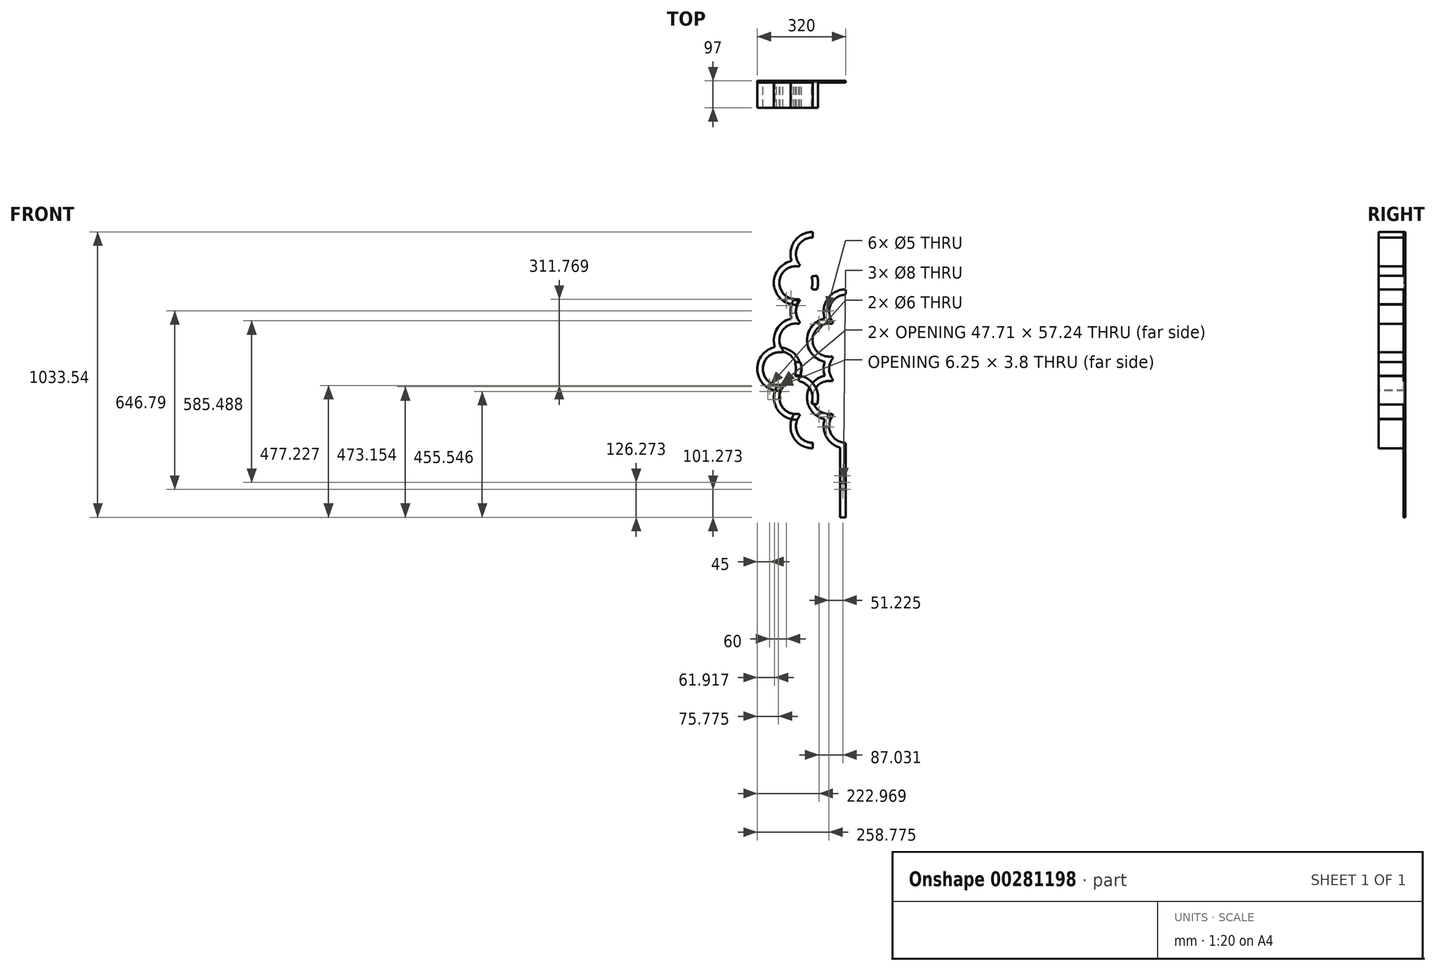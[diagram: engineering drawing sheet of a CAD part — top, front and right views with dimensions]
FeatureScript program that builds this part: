
annotation { "Feature Type Name" : "Feature", "Feature Type Description" : "" }
export const myFeature = defineFeature(function(context is Context, id is Id, definition is map)
    precondition{}
    {
        {
            var Q0;
            Q0=qCreatedBy(makeId("Front.planeOp"),FACE);
            var sketch = newSketch(context, id + "F0", { "sketchPlane" : qUnion([Q0])});
            skCircle(sketch, "E0.1.0.0", {"center": v(-79.6, 28.75) * mm, "radius": 60 * mm, "construction": true});
            skCircle(sketch, "E0.2.0.0", {"center": v(40.4, 28.75) * mm, "radius": 60 * mm, "construction": true});
            skCircle(sketch, "E0.3.0.0", {"center": v(160.4, 28.75) * mm, "radius": 60 * mm, "construction": true});
            skLineSegment(sketch, "E0.direction1", {"start": v(-199.6, 28.75) * mm, "end": v(-79.6, 28.75) * mm, "construction": true});
            skCircle(sketch, "E1", {"center": v(-139.6, 132.68) * mm, "radius": 60 * mm, "construction": true});
            skCircle(sketch, "E2.1.0.0", {"center": v(-19.6, 132.68) * mm, "radius": 60 * mm, "construction": true});
            skCircle(sketch, "E2.2.0.0", {"center": v(100.4, 132.68) * mm, "radius": 60 * mm, "construction": true});
            skCircle(sketch, "E2.3.0.0", {"center": v(220.4, 132.68) * mm, "radius": 60 * mm, "construction": true});
            skLineSegment(sketch, "E2.direction1", {"start": v(-139.6, 132.68) * mm, "end": v(-19.6, 132.68) * mm, "construction": true});
            skCircle(sketch, "E3", {"center": v(-199.6, 236.6) * mm, "radius": 60 * mm, "construction": true});
            skCircle(sketch, "E4", {"center": v(-139.6, 340.52) * mm, "radius": 60 * mm, "construction": true});
            skCircle(sketch, "E5.1.0.0", {"center": v(-79.6, 236.6) * mm, "radius": 60 * mm, "construction": true});
            skCircle(sketch, "E5.1.0.1", {"center": v(-19.6, 340.52) * mm, "radius": 60 * mm, "construction": true});
            skCircle(sketch, "E5.2.0.0", {"center": v(40.4, 236.6) * mm, "radius": 60 * mm, "construction": true});
            skCircle(sketch, "E5.2.0.1", {"center": v(100.4, 340.52) * mm, "radius": 60 * mm, "construction": true});
            skCircle(sketch, "E5.3.0.0", {"center": v(160.4, 236.6) * mm, "radius": 60 * mm, "construction": true});
            skCircle(sketch, "E5.3.0.1", {"center": v(220.4, 340.52) * mm, "radius": 60 * mm, "construction": true});
            skLineSegment(sketch, "E5.direction1", {"start": v(-199.6, 236.6) * mm, "end": v(-79.6, 236.6) * mm, "construction": true});
            skCircle(sketch, "E6.0.4.0", {"center": v(280.4, 28.75) * mm, "radius": 60 * mm, "construction": true});
            skCircle(sketch, "E7.0.4.0", {"center": v(340.4, 132.68) * mm, "radius": 60 * mm, "construction": true});
            skCircle(sketch, "E8.0.4.0", {"center": v(280.4, 236.6) * mm, "radius": 60 * mm, "construction": true});
            skCircle(sketch, "E8.2.4.0", {"center": v(340.4, 340.52) * mm, "radius": 60 * mm, "construction": true});
            skCircle(sketch, "E9.1.0.0", {"center": v(-79.6, 444.44) * mm, "radius": 60 * mm, "construction": true});
            skCircle(sketch, "E9.2.0.0", {"center": v(40.4, 444.44) * mm, "radius": 60 * mm, "construction": true});
            skCircle(sketch, "E9.3.0.0", {"center": v(160.4, 444.44) * mm, "radius": 60 * mm, "construction": true});
            skCircle(sketch, "E9.4.0.0", {"center": v(280.4, 444.44) * mm, "radius": 60 * mm, "construction": true});
            skLineSegment(sketch, "E9.direction1", {"start": v(-199.6, 444.44) * mm, "end": v(-79.6, 444.44) * mm, "construction": true});
            skCircle(sketch, "E10", {"center": v(-139.6, 548.37) * mm, "radius": 60 * mm, "construction": true});
            skCircle(sketch, "E11.1.0.0", {"center": v(-19.6, 548.37) * mm, "radius": 60 * mm, "construction": true});
            skCircle(sketch, "E11.1.0.1", {"center": v(-79.6, 652.3) * mm, "radius": 60 * mm, "construction": true});
            skCircle(sketch, "E11.2.0.0", {"center": v(100.4, 548.37) * mm, "radius": 60 * mm, "construction": true});
            skCircle(sketch, "E11.2.0.1", {"center": v(40.4, 652.3) * mm, "radius": 60 * mm, "construction": true});
            skCircle(sketch, "E11.3.0.0", {"center": v(220.4, 548.37) * mm, "radius": 60 * mm, "construction": true});
            skCircle(sketch, "E11.3.0.1", {"center": v(160.4, 652.3) * mm, "radius": 60 * mm, "construction": true});
            skCircle(sketch, "E11.4.0.0", {"center": v(340.4, 548.37) * mm, "radius": 60 * mm, "construction": true});
            skCircle(sketch, "E11.4.0.1", {"center": v(280.4, 652.3) * mm, "radius": 60 * mm, "construction": true});
            skLineSegment(sketch, "E11.direction1", {"start": v(-139.6, 548.37) * mm, "end": v(-19.6, 548.37) * mm, "construction": true});
            skSolve(sketch);
        }
        {
            var Q0;
            Q0=qCreatedBy(makeId("Front.planeOp"),FACE);
            var sketch = newSketch(context, id + "F1", { "sketchPlane" : qUnion([Q0])});
            skCircle(sketch, "E12.0", {"center": v(-199.6, 236.6) * mm, "radius": 60 * mm});
            skCircle(sketch, "E13.0", {"center": v(-139.6, 340.52) * mm, "radius": 60 * mm});
            skCircle(sketch, "E14.0", {"center": v(-139.6, 132.68) * mm, "radius": 60 * mm});
            skCircle(sketch, "E15.0", {"center": v(-79.6, 28.75) * mm, "radius": 60 * mm});
            skCircle(sketch, "E16.0", {"center": v(-139.6, 548.37) * mm, "radius": 60 * mm});
            skCircle(sketch, "E17.0", {"center": v(-79.6, 444.44) * mm, "radius": 60 * mm});
            skCircle(sketch, "E18.0", {"center": v(-79.6, 652.3) * mm, "radius": 60 * mm});
            skCircle(sketch, "E19", {"center": v(-79.6, 652.3) * mm, "radius": 80 * mm});
            skCircle(sketch, "E20", {"center": v(-139.6, 548.37) * mm, "radius": 80 * mm});
            skCircle(sketch, "E21", {"center": v(-79.6, 444.44) * mm, "radius": 80 * mm});
            skCircle(sketch, "E22", {"center": v(-139.6, 340.52) * mm, "radius": 80 * mm});
            skCircle(sketch, "E23", {"center": v(-199.6, 236.6) * mm, "radius": 80 * mm});
            skCircle(sketch, "E24", {"center": v(-139.6, 132.68) * mm, "radius": 80 * mm});
            skCircle(sketch, "E25", {"center": v(-79.6, 28.75) * mm, "radius": 80 * mm});
            skLineSegment(sketch, "E26", {"start": v(-79.6, 28.75) * mm, "end": v(-79.6, -51.25) * mm});
            skLineSegment(sketch, "E27", {"start": v(-79.6, 652.3) * mm, "end": v(-79.6, 732.3) * mm});
            skSolve(sketch);
        }
        {
            var Q0;
            {var subQ0=sQuery(id+"F1.wireOp",EDGE,"E27");var subQ1=sQuery(id+"F1.wireOp",EDGE,"E18.0");var subQ2=makeQuery(id+"F1.imprint","INTERSECT",VERTEX,{"derivedFrom":[subQ1,subQ0]});Q0=makeQuery(id+"F1.imprint","IMPRINT",FACE,{"disambiguationData":[TD([[makeQuery(id+"F1.imprint","IMPRINT",EDGE,{"disambiguationData":[TD([[subQ2,-1.0]])],"derivedFrom":subQ1}),-1.0]])]});}
            var Q1;
            {var subQ0=sQuery(id+"F1.wireOp",EDGE,"E18.0");var subQ1=sQuery(id+"F1.wireOp",EDGE,"E16.0");var subQ2=makeQuery(id+"F1.imprint","INTERSECT",VERTEX,{"derivedFrom":[subQ1,subQ0]});Q1=makeQuery(id+"F1.imprint","IMPRINT",FACE,{"disambiguationData":[TD([[makeQuery(id+"F1.imprint","IMPRINT",EDGE,{"disambiguationData":[TD([[subQ2,-1.0]])],"derivedFrom":subQ1}),-1.0]])]});}
            var Q2;
            {var subQ0=sQuery(id+"F1.wireOp",EDGE,"E19");var subQ1=sQuery(id+"F1.wireOp",EDGE,"E16.0");var subQ2=makeQuery(id+"F1.imprint","INTERSECT",VERTEX,{"disambiguationData":[OD(1.0)],"derivedFrom":[subQ1,subQ0]});Q2=makeQuery(id+"F1.imprint","IMPRINT",FACE,{"disambiguationData":[TD([[makeQuery(id+"F1.imprint","IMPRINT",EDGE,{"disambiguationData":[TD([[subQ2,-1.0]])],"derivedFrom":subQ1}),-1.0]])]});}
            var Q3;
            {var subQ0=sQuery(id+"F1.wireOp",EDGE,"E20");var subQ1=sQuery(id+"F1.wireOp",EDGE,"E17.0");var subQ2=makeQuery(id+"F1.imprint","INTERSECT",VERTEX,{"disambiguationData":[OD(1.0)],"derivedFrom":[subQ1,subQ0]});Q3=makeQuery(id+"F1.imprint","IMPRINT",FACE,{"disambiguationData":[TD([[makeQuery(id+"F1.imprint","IMPRINT",EDGE,{"disambiguationData":[TD([[subQ2,-1.0]])],"derivedFrom":subQ1}),-1.0]])]});}
            var Q4;
            {var subQ0=sQuery(id+"F1.wireOp",EDGE,"E21");var subQ1=sQuery(id+"F1.wireOp",EDGE,"E16.0");var subQ2=makeQuery(id+"F1.imprint","INTERSECT",VERTEX,{"disambiguationData":[OD(0.0)],"derivedFrom":[subQ1,subQ0]});Q4=makeQuery(id+"F1.imprint","IMPRINT",FACE,{"disambiguationData":[TD([[makeQuery(id+"F1.imprint","IMPRINT",EDGE,{"disambiguationData":[TD([[subQ2,-1.0]])],"derivedFrom":subQ1}),-1.0]])]});}
            var Q5;
            {var subQ0=sQuery(id+"F1.wireOp",EDGE,"E21");var subQ1=sQuery(id+"F1.wireOp",EDGE,"E13.0");var subQ2=makeQuery(id+"F1.imprint","INTERSECT",VERTEX,{"disambiguationData":[OD(1.0)],"derivedFrom":[subQ1,subQ0]});Q5=makeQuery(id+"F1.imprint","IMPRINT",FACE,{"disambiguationData":[TD([[makeQuery(id+"F1.imprint","IMPRINT",EDGE,{"disambiguationData":[TD([[subQ2,-1.0]])],"derivedFrom":subQ1}),-1.0]])]});}
            var Q6;
            {var subQ0=sQuery(id+"F1.wireOp",EDGE,"E17.0");var subQ1=sQuery(id+"F1.wireOp",EDGE,"E13.0");var subQ2=makeQuery(id+"F1.imprint","INTERSECT",VERTEX,{"derivedFrom":[subQ1,subQ0]});Q6=makeQuery(id+"F1.imprint","IMPRINT",FACE,{"disambiguationData":[TD([[makeQuery(id+"F1.imprint","IMPRINT",EDGE,{"disambiguationData":[TD([[subQ2,-1.0]])],"derivedFrom":subQ1}),-1.0]])]});}
            var Q7;
            {var subQ0=sQuery(id+"F1.wireOp",EDGE,"E13.0");var subQ1=sQuery(id+"F1.wireOp",EDGE,"E12.0");var subQ2=makeQuery(id+"F1.imprint","INTERSECT",VERTEX,{"derivedFrom":[subQ1,subQ0]});Q7=makeQuery(id+"F1.imprint","IMPRINT",FACE,{"disambiguationData":[TD([[makeQuery(id+"F1.imprint","IMPRINT",EDGE,{"disambiguationData":[TD([[subQ2,-1.0]])],"derivedFrom":subQ1}),-1.0]])]});}
            var Q8;
            {var subQ0=sQuery(id+"F1.wireOp",EDGE,"E22");var subQ1=sQuery(id+"F1.wireOp",EDGE,"E12.0");var subQ2=makeQuery(id+"F1.imprint","INTERSECT",VERTEX,{"disambiguationData":[OD(1.0)],"derivedFrom":[subQ1,subQ0]});Q8=makeQuery(id+"F1.imprint","IMPRINT",FACE,{"disambiguationData":[TD([[makeQuery(id+"F1.imprint","IMPRINT",EDGE,{"disambiguationData":[TD([[subQ2,-1.0]])],"derivedFrom":subQ1}),-1.0]])]});}
            var Q9;
            {var subQ0=sQuery(id+"F1.wireOp",EDGE,"E23");var subQ1=sQuery(id+"F1.wireOp",EDGE,"E14.0");var subQ2=makeQuery(id+"F1.imprint","INTERSECT",VERTEX,{"disambiguationData":[OD(1.0)],"derivedFrom":[subQ1,subQ0]});Q9=makeQuery(id+"F1.imprint","IMPRINT",FACE,{"disambiguationData":[TD([[makeQuery(id+"F1.imprint","IMPRINT",EDGE,{"disambiguationData":[TD([[subQ2,-1.0]])],"derivedFrom":subQ1}),-1.0]])]});}
            var Q10;
            {var subQ0=sQuery(id+"F1.wireOp",EDGE,"E26");var subQ1=sQuery(id+"F1.wireOp",EDGE,"E15.0");var subQ2=makeQuery(id+"F1.imprint","INTERSECT",VERTEX,{"derivedFrom":[subQ1,subQ0]});Q10=makeQuery(id+"F1.imprint","IMPRINT",FACE,{"disambiguationData":[TD([[makeQuery(id+"F1.imprint","IMPRINT",EDGE,{"disambiguationData":[TD([[subQ2,1.0]])],"derivedFrom":subQ1}),-1.0]])]});}
            var Q11;
            {var subQ0=sQuery(id+"F1.wireOp",EDGE,"E25");var subQ1=sQuery(id+"F1.wireOp",EDGE,"E14.0");var subQ2=makeQuery(id+"F1.imprint","INTERSECT",VERTEX,{"disambiguationData":[OD(0.0)],"derivedFrom":[subQ1,subQ0]});Q11=makeQuery(id+"F1.imprint","IMPRINT",FACE,{"disambiguationData":[TD([[makeQuery(id+"F1.imprint","IMPRINT",EDGE,{"disambiguationData":[TD([[subQ2,-1.0]])],"derivedFrom":subQ1}),-1.0]])]});}
            var Q12;
            {var subQ0=sQuery(id+"F1.wireOp",EDGE,"E24");var subQ1=sQuery(id+"F1.wireOp",EDGE,"E12.0");var subQ2=makeQuery(id+"F1.imprint","INTERSECT",VERTEX,{"disambiguationData":[OD(0.0)],"derivedFrom":[subQ1,subQ0]});Q12=makeQuery(id+"F1.imprint","IMPRINT",FACE,{"disambiguationData":[TD([[makeQuery(id+"F1.imprint","IMPRINT",EDGE,{"disambiguationData":[TD([[subQ2,-1.0]])],"derivedFrom":subQ1}),-1.0]])]});}
            extrude(context, id + "F2", {"entities" : qUnion([Q0, Q1, Q2, Q3, Q4, Q5, Q6, Q7, Q8, Q9, Q10, Q11, Q12]), "depth" : 97 * mm});
        }
        {
            var Q0;
            Q0=makeQuery(id+"F2.opExtrude","SWEPT_EDGE",EDGE,{"disambiguationData":[OSD([sQuery(id+"F1.wireOp",EDGE,"E16.0"),sQuery(id+"F1.wireOp",EDGE,"E18.0")])]});
            var Q1;
            Q1=makeQuery(id+"F2.opExtrude","SWEPT_EDGE",EDGE,{"disambiguationData":[OSD([sQuery(id+"F1.wireOp",EDGE,"E16.0"),sQuery(id+"F1.wireOp",EDGE,"E17.0")])]});
            var Q2;
            Q2=makeQuery(id+"F2.opExtrude","SWEPT_EDGE",EDGE,{"disambiguationData":[OSD([sQuery(id+"F1.wireOp",EDGE,"E13.0"),sQuery(id+"F1.wireOp",EDGE,"E17.0")])]});
            var Q3;
            Q3=makeQuery(id+"F2.opExtrude","SWEPT_EDGE",EDGE,{"disambiguationData":[OSD([sQuery(id+"F1.wireOp",EDGE,"E12.0"),sQuery(id+"F1.wireOp",EDGE,"E13.0")])]});
            var Q4;
            Q4=makeQuery(id+"F2.opExtrude","SWEPT_EDGE",EDGE,{"disambiguationData":[OSD([sQuery(id+"F1.wireOp",EDGE,"E12.0"),sQuery(id+"F1.wireOp",EDGE,"E14.0")])]});
            var Q5;
            Q5=makeQuery(id+"F2.opExtrude","SWEPT_EDGE",EDGE,{"disambiguationData":[OSD([sQuery(id+"F1.wireOp",EDGE,"E14.0"),sQuery(id+"F1.wireOp",EDGE,"E15.0")])]});
            var Q6;
            Q6=makeQuery(id+"F2.opExtrude","SWEPT_EDGE",EDGE,{"disambiguationData":[OSD([sQuery(id+"F1.wireOp",EDGE,"E19"),sQuery(id+"F1.wireOp",EDGE,"E20")])]});
            var Q7;
            Q7=makeQuery(id+"F2.opExtrude","SWEPT_EDGE",EDGE,{"disambiguationData":[OSD([sQuery(id+"F1.wireOp",EDGE,"E21"),sQuery(id+"F1.wireOp",EDGE,"E22")])]});
            var Q8;
            Q8=makeQuery(id+"F2.opExtrude","SWEPT_EDGE",EDGE,{"disambiguationData":[OSD([sQuery(id+"F1.wireOp",EDGE,"E22"),sQuery(id+"F1.wireOp",EDGE,"E23")])]});
            var Q9;
            Q9=makeQuery(id+"F2.opExtrude","SWEPT_EDGE",EDGE,{"disambiguationData":[OSD([sQuery(id+"F1.wireOp",EDGE,"E20"),sQuery(id+"F1.wireOp",EDGE,"E21")])]});
            var Q10;
            Q10=makeQuery(id+"F2.opExtrude","SWEPT_EDGE",EDGE,{"disambiguationData":[OSD([sQuery(id+"F1.wireOp",EDGE,"E23"),sQuery(id+"F1.wireOp",EDGE,"E24")])]});
            var Q11;
            Q11=makeQuery(id+"F2.opExtrude","SWEPT_EDGE",EDGE,{"disambiguationData":[OSD([sQuery(id+"F1.wireOp",EDGE,"E24"),sQuery(id+"F1.wireOp",EDGE,"E25")])]});
            fillet(context, id + "F3", {"entities" : qUnion([Q0, Q1, Q2, Q3, Q4, Q5, Q6, Q7, Q8, Q9, Q10, Q11]), "radius" : 5 * mm, "tangentPropagation" : true, "allowEdgeOverflow" : false});
        }
        {
            var Q0;
            Q0=qCreatedBy(makeId("Front.planeOp"),FACE);
            var sketch = newSketch(context, id + "F4", { "sketchPlane" : qUnion([Q0])});
            skArc(sketch, "E28.0", {"start": v(-79.6, 732.3) * mm, "mid": v(-144.55, 698.98) * mm, "end": v(-155.42, 626.79) * mm});
            skArc(sketch, "E28.1", {"start": v(-79.6, 712.3) * mm, "mid": v(-133.37, 678.88) * mm, "end": v(-127.27, 615.86) * mm});
            skArc(sketch, "E28.2", {"start": v(-131.88, 607.87) * mm, "mid": v(-199.6, 548.37) * mm, "end": v(-131.88, 488.86) * mm});
            skArc(sketch, "E28.5", {"start": v(-127.27, 480.87) * mm, "mid": v(-139.6, 444.44) * mm, "end": v(-127.27, 408.02) * mm});
            skArc(sketch, "E28.6", {"start": v(-155.42, 418.94) * mm, "mid": v(-208.87, 380.52) * mm, "end": v(-215.42, 315.02) * mm});
            skArc(sketch, "E28.7", {"start": v(-131.88, 400.02) * mm, "mid": v(-191.55, 370.52) * mm, "end": v(-187.27, 304.1) * mm});
            skArc(sketch, "E28.8", {"start": v(-215.42, 315.02) * mm, "mid": v(-279.6, 236.6) * mm, "end": v(-215.42, 158.18) * mm});
            skArc(sketch, "E28.9", {"start": v(-191.88, 296.1) * mm, "mid": v(-259.6, 236.6) * mm, "end": v(-191.88, 177.1) * mm});
            skArc(sketch, "E28.10", {"start": v(-215.42, 158.18) * mm, "mid": v(-208.87, 92.68) * mm, "end": v(-155.42, 54.26) * mm});
            skArc(sketch, "E28.11", {"start": v(-187.27, 169.1) * mm, "mid": v(-191.55, 102.68) * mm, "end": v(-131.88, 73.17) * mm});
            skArc(sketch, "E28.12", {"start": v(-155.42, 54.26) * mm, "mid": v(-144.55, -17.94) * mm, "end": v(-79.6, -51.25) * mm});
            skArc(sketch, "E28.13", {"start": v(-127.27, 65.18) * mm, "mid": v(-133.37, 2.16) * mm, "end": v(-79.6, -31.25) * mm});
            skLineSegment(sketch, "E29.0", {"start": v(-79.6, 652.3) * mm, "end": v(-79.6, 732.3) * mm});
            skLineSegment(sketch, "E30.0", {"start": v(-79.6, -31.25) * mm, "end": v(-79.6, -51.25) * mm});
            skArc(sketch, "E31.trimOffspring", {"start": v(-155.42, 626.79) * mm, "mid": v(-219.6, 548.37) * mm, "end": v(-155.42, 469.95) * mm});
            skArc(sketch, "E32.trimOffspring", {"start": v(-155.42, 469.95) * mm, "mid": v(-159.6, 444.44) * mm, "end": v(-155.42, 418.94) * mm});
            skPoint(sketch, "E33.visualSharp", {"position": v(-109.6, 496.4) * mm});
            skCircle(sketch, "E34", {"center": v(-199.6, 236.6) * mm, "radius": 70 * mm, "construction": true});
            skCircle(sketch, "E35", {"center": v(-139.6, 132.68) * mm, "radius": 70 * mm, "construction": true});
            skPoint(sketch, "E36.visualSharp", {"position": v(-169.6, 184.64) * mm});
            skPoint(sketch, "E37.visualSharp", {"position": v(-109.6, 80.71) * mm});
            skArc(sketch, "E37.filletArc", {"start": v(-127.27, 65.18) * mm, "mid": v(-126.91, 70.71) * mm, "end": v(-131.88, 73.17) * mm});
            skArc(sketch, "E38.filletArc", {"start": v(-187.27, 169.1) * mm, "mid": v(-186.91, 174.64) * mm, "end": v(-191.88, 177.1) * mm});
            skPoint(sketch, "E39.visualSharp", {"position": v(-169.6, 288.56) * mm});
            skArc(sketch, "E39.filletArc", {"start": v(-191.88, 296.1) * mm, "mid": v(-186.91, 298.56) * mm, "end": v(-187.27, 304.1) * mm});
            skPoint(sketch, "E40.visualSharp", {"position": v(-109.6, 392.48) * mm});
            skArc(sketch, "E40.filletArc", {"start": v(-131.88, 400.02) * mm, "mid": v(-126.91, 402.48) * mm, "end": v(-127.27, 408.02) * mm});
            skArc(sketch, "E41.filletArc", {"start": v(-127.27, 480.87) * mm, "mid": v(-126.91, 486.4) * mm, "end": v(-131.88, 488.86) * mm});
            skPoint(sketch, "E42.visualSharp", {"position": v(-109.6, 600.33) * mm});
            skArc(sketch, "E42.filletArc", {"start": v(-131.88, 607.87) * mm, "mid": v(-126.91, 610.33) * mm, "end": v(-127.27, 615.86) * mm});
            skCircle(sketch, "E43", {"center": v(-79.6, 444.44) * mm, "radius": 63 * mm});
            skCircle(sketch, "E44", {"center": v(-79.6, 444.44) * mm, "radius": 77 * mm});
            skCircle(sketch, "E45", {"center": v(-199.6, 236.6) * mm, "radius": 63 * mm});
            skCircle(sketch, "E46", {"center": v(-199.6, 236.6) * mm, "radius": 77 * mm});
            skCircle(sketch, "E47", {"center": v(-139.6, 132.68) * mm, "radius": 63 * mm});
            skCircle(sketch, "E48", {"center": v(-139.6, 132.68) * mm, "radius": 77 * mm});
            skCircle(sketch, "E49", {"center": v(-200.82, 166.6) * mm, "radius": 7 * mm});
            skCircle(sketch, "E50", {"center": v(-139.6, 548.37) * mm, "radius": 63 * mm});
            skCircle(sketch, "E51", {"center": v(-139.6, 548.37) * mm, "radius": 77 * mm});
            skCircle(sketch, "E52", {"center": v(-79.6, 444.44) * mm, "radius": 70 * mm, "construction": true});
            skCircle(sketch, "E53", {"center": v(-139.6, 548.37) * mm, "radius": 70 * mm, "construction": true});
            skCircle(sketch, "E54", {"center": v(-140.82, 478.38) * mm, "radius": 7 * mm});
            skArc(sketch, "E55", {"start": v(-156.6, 444.44) * mm, "mid": v(-149.6, 437.44) * mm, "end": v(-142.6, 444.44) * mm});
            skArc(sketch, "E56", {"start": v(-171.1, 493.8) * mm, "mid": v(-180.65, 491.25) * mm, "end": v(-178.1, 481.68) * mm});
            skArc(sketch, "E57", {"start": v(-216.6, 132.68) * mm, "mid": v(-209.6, 125.68) * mm, "end": v(-202.6, 132.68) * mm});
            skArc(sketch, "E58", {"start": v(-231.1, 182.04) * mm, "mid": v(-240.65, 179.48) * mm, "end": v(-238.1, 169.91) * mm});
            skCircle(sketch, "E59", {"center": v(-174.6, 487.75) * mm, "radius": 3 * mm});
            skCircle(sketch, "E60", {"center": v(-234.6, 175.98) * mm, "radius": 3 * mm});
            skSolve(sketch);
        }
        {
            var Q0;
            {var subQ8=sQuery(id+"F4.wireOp",EDGE,"E28.0");Q0=makeQuery(id+"F4.imprint","IMPRINT",FACE,{"disambiguationData":[TD([[makeQuery(id+"F4.imprint","IMPRINT",EDGE,{"derivedFrom":subQ8}),1.0]])]});}
            var Q1;
            {var subQ0=sQuery(id+"F4.wireOp",EDGE,"E56");Q1=makeQuery(id+"F4.imprint","IMPRINT",FACE,{"disambiguationData":[TD([[makeQuery(id+"F4.imprint","IMPRINT",EDGE,{"derivedFrom":subQ0}),-1.0]])]});}
            var Q2;
            {var subQ2=sQuery(id+"F4.wireOp",EDGE,"E42.filletArc");var subQ4=sQuery(id+"F4.wireOp",EDGE,"E28.2");var subQ5=makeQuery(id+"F4.imprint","INTERSECT",VERTEX,{"derivedFrom":[subQ4,subQ2]});Q2=makeQuery(id+"F4.imprint","IMPRINT",FACE,{"disambiguationData":[TD([[makeQuery(id+"F4.imprint","IMPRINT",EDGE,{"disambiguationData":[TD([[subQ5,-1.0]])],"derivedFrom":subQ4}),-1.0]])]});}
            var Q3;
            {var subQ4=sQuery(id+"F4.wireOp",EDGE,"E28.2");var subQ6=sQuery(id+"F4.wireOp",EDGE,"E41.filletArc");var subQ7=makeQuery(id+"F4.imprint","INTERSECT",VERTEX,{"derivedFrom":[subQ4,subQ6]});Q3=makeQuery(id+"F4.imprint","IMPRINT",FACE,{"disambiguationData":[TD([[makeQuery(id+"F4.imprint","IMPRINT",EDGE,{"disambiguationData":[TD([[subQ7,1.0]])],"derivedFrom":subQ4}),-1.0]])]});}
            var Q4;
            {var subQ0=sQuery(id+"F4.wireOp",EDGE,"E43");var subQ1=sQuery(id+"F4.wireOp",EDGE,"E41.filletArc");var subQ2=makeQuery(id+"F4.imprint","INTERSECT",VERTEX,{"derivedFrom":[subQ1,subQ0]});Q4=makeQuery(id+"F4.imprint","IMPRINT",FACE,{"disambiguationData":[TD([[makeQuery(id+"F4.imprint","IMPRINT",EDGE,{"disambiguationData":[TD([[subQ2,-1.0]])],"derivedFrom":subQ1}),1.0]])]});}
            var Q5;
            {var subQ4=sQuery(id+"F4.wireOp",EDGE,"E41.filletArc");var subQ6=sQuery(id+"F4.wireOp",EDGE,"E28.5");var subQ7=makeQuery(id+"F4.imprint","INTERSECT",VERTEX,{"derivedFrom":[subQ6,subQ4]});Q5=makeQuery(id+"F4.imprint","IMPRINT",FACE,{"disambiguationData":[TD([[makeQuery(id+"F4.imprint","IMPRINT",EDGE,{"disambiguationData":[TD([[subQ7,-1.0]])],"derivedFrom":subQ6}),-1.0]])]});}
            var Q6;
            {var subQ2=sQuery(id+"F4.wireOp",EDGE,"E40.filletArc");var subQ6=sQuery(id+"F4.wireOp",EDGE,"E28.5");var subQ7=makeQuery(id+"F4.imprint","INTERSECT",VERTEX,{"derivedFrom":[subQ6,subQ2]});Q6=makeQuery(id+"F4.imprint","IMPRINT",FACE,{"disambiguationData":[TD([[makeQuery(id+"F4.imprint","IMPRINT",EDGE,{"disambiguationData":[TD([[subQ7,1.0]])],"derivedFrom":subQ6}),-1.0]])]});}
            var Q7;
            {var subQ0=sQuery(id+"F4.wireOp",EDGE,"E55");Q7=makeQuery(id+"F4.imprint","IMPRINT",FACE,{"disambiguationData":[TD([[makeQuery(id+"F4.imprint","IMPRINT",EDGE,{"derivedFrom":subQ0}),-1.0]])]});}
            var Q8;
            {var subQ0=sQuery(id+"F4.wireOp",EDGE,"E58");Q8=makeQuery(id+"F4.imprint","IMPRINT",FACE,{"disambiguationData":[TD([[makeQuery(id+"F4.imprint","IMPRINT",EDGE,{"derivedFrom":subQ0}),-1.0]])]});}
            var Q9;
            {var subQ4=sQuery(id+"F4.wireOp",EDGE,"E39.filletArc");var subQ6=sQuery(id+"F4.wireOp",EDGE,"E28.9");var subQ7=makeQuery(id+"F4.imprint","INTERSECT",VERTEX,{"derivedFrom":[subQ6,subQ4]});Q9=makeQuery(id+"F4.imprint","IMPRINT",FACE,{"disambiguationData":[TD([[makeQuery(id+"F4.imprint","IMPRINT",EDGE,{"disambiguationData":[TD([[subQ7,-1.0]])],"derivedFrom":subQ6}),-1.0]])]});}
            var Q10;
            {var subQ4=sQuery(id+"F4.wireOp",EDGE,"E37.filletArc");var subQ5=sQuery(id+"F4.wireOp",EDGE,"E28.11");var subQ6=makeQuery(id+"F4.imprint","INTERSECT",VERTEX,{"derivedFrom":[subQ5,subQ4]});Q10=makeQuery(id+"F4.imprint","IMPRINT",FACE,{"disambiguationData":[TD([[makeQuery(id+"F4.imprint","IMPRINT",EDGE,{"disambiguationData":[TD([[subQ6,1.0]])],"derivedFrom":subQ5}),-1.0]])]});}
            var Q11;
            {var subQ1=sQuery(id+"F4.wireOp",EDGE,"E38.filletArc");var subQ5=sQuery(id+"F4.wireOp",EDGE,"E28.11");var subQ8=makeQuery(id+"F4.imprint","INTERSECT",VERTEX,{"derivedFrom":[subQ5,subQ1]});Q11=makeQuery(id+"F4.imprint","IMPRINT",FACE,{"disambiguationData":[TD([[makeQuery(id+"F4.imprint","IMPRINT",EDGE,{"disambiguationData":[TD([[subQ8,-1.0]])],"derivedFrom":subQ5}),-1.0]])]});}
            var Q12;
            {var subQ1=sQuery(id+"F4.wireOp",EDGE,"E38.filletArc");var subQ4=sQuery(id+"F4.wireOp",EDGE,"E28.9");var subQ5=makeQuery(id+"F4.imprint","INTERSECT",VERTEX,{"derivedFrom":[subQ4,subQ1]});Q12=makeQuery(id+"F4.imprint","IMPRINT",FACE,{"disambiguationData":[TD([[makeQuery(id+"F4.imprint","IMPRINT",EDGE,{"disambiguationData":[TD([[subQ5,1.0]])],"derivedFrom":subQ4}),-1.0]])]});}
            var Q13;
            {var subQ0=sQuery(id+"F4.wireOp",EDGE,"E47");var subQ1=sQuery(id+"F4.wireOp",EDGE,"E38.filletArc");var subQ2=makeQuery(id+"F4.imprint","INTERSECT",VERTEX,{"derivedFrom":[subQ1,subQ0]});Q13=makeQuery(id+"F4.imprint","IMPRINT",FACE,{"disambiguationData":[TD([[makeQuery(id+"F4.imprint","IMPRINT",EDGE,{"disambiguationData":[TD([[subQ2,-1.0]])],"derivedFrom":subQ1}),1.0]])]});}
            var Q14;
            {var subQ0=sQuery(id+"F4.wireOp",EDGE,"E57");Q14=makeQuery(id+"F4.imprint","IMPRINT",FACE,{"disambiguationData":[TD([[makeQuery(id+"F4.imprint","IMPRINT",EDGE,{"derivedFrom":subQ0}),-1.0]])]});}
            extrude(context, id + "F5", {"entities" : qUnion([Q0, Q1, Q2, Q3, Q4, Q5, Q6, Q7, Q8, Q9, Q10, Q11, Q12, Q13, Q14]), "depth" : 6 * mm});
        }
        {
            var Q0;
            {var subQ0=sQuery(id+"F4.wireOp",EDGE,"E56");Q0=makeQuery(id+"F4.imprint","IMPRINT",FACE,{"disambiguationData":[TD([[makeQuery(id+"F4.imprint","IMPRINT",EDGE,{"derivedFrom":subQ0}),1.0]])]});}
            var Q1;
            {var subQ0=sQuery(id+"F4.wireOp",EDGE,"E54");var subQ1=makeQuery(id+"F4.imprint","INTERSECT",VERTEX,{"derivedFrom":[sQuery(id+"F4.wireOp",EDGE,"E44"),subQ0]});Q1=makeQuery(id+"F4.imprint","IMPRINT",FACE,{"disambiguationData":[TD([[makeQuery(id+"F4.imprint","IMPRINT",EDGE,{"disambiguationData":[TD([[subQ1,1.0]])],"derivedFrom":subQ0}),1.0]])]});}
            var Q2;
            {var subQ6=sQuery(id+"F4.wireOp",EDGE,"E55");Q2=makeQuery(id+"F4.imprint","IMPRINT",FACE,{"disambiguationData":[TD([[makeQuery(id+"F4.imprint","IMPRINT",EDGE,{"derivedFrom":subQ6}),1.0]])]});}
            var Q3;
            {var subQ0=sQuery(id+"F4.wireOp",EDGE,"E50");var subQ1=sQuery(id+"F4.wireOp",EDGE,"E44");var subQ2=makeQuery(id+"F4.imprint","INTERSECT",VERTEX,{"disambiguationData":[OD(1.0)],"derivedFrom":[subQ1,subQ0]});Q3=makeQuery(id+"F4.imprint","IMPRINT",FACE,{"disambiguationData":[TD([[makeQuery(id+"F4.imprint","IMPRINT",EDGE,{"disambiguationData":[TD([[subQ2,-1.0]])],"derivedFrom":subQ1}),1.0]])]});}
            var Q4;
            {var subQ0=sQuery(id+"F4.wireOp",EDGE,"E54");var subQ1=sQuery(id+"F4.wireOp",EDGE,"E44");var subQ2=makeQuery(id+"F4.imprint","INTERSECT",VERTEX,{"derivedFrom":[subQ1,subQ0]});Q4=makeQuery(id+"F4.imprint","IMPRINT",FACE,{"disambiguationData":[TD([[makeQuery(id+"F4.imprint","IMPRINT",EDGE,{"disambiguationData":[TD([[subQ2,-1.0]])],"derivedFrom":subQ1}),1.0]])]});}
            var Q5;
            {var subQ0=sQuery(id+"F4.wireOp",EDGE,"E54");var subQ1=sQuery(id+"F4.wireOp",EDGE,"E43");var subQ2=makeQuery(id+"F4.imprint","INTERSECT",VERTEX,{"derivedFrom":[subQ1,subQ0]});Q5=makeQuery(id+"F4.imprint","IMPRINT",FACE,{"disambiguationData":[TD([[makeQuery(id+"F4.imprint","IMPRINT",EDGE,{"disambiguationData":[TD([[subQ2,-1.0]])],"derivedFrom":subQ1}),-1.0]])]});}
            var Q6;
            {var subQ6=sQuery(id+"F4.wireOp",EDGE,"E58");Q6=makeQuery(id+"F4.imprint","IMPRINT",FACE,{"disambiguationData":[TD([[makeQuery(id+"F4.imprint","IMPRINT",EDGE,{"derivedFrom":subQ6}),1.0]])]});}
            var Q7;
            {var subQ0=sQuery(id+"F4.wireOp",EDGE,"E49");var subQ1=makeQuery(id+"F4.imprint","INTERSECT",VERTEX,{"derivedFrom":[sQuery(id+"F4.wireOp",EDGE,"E45"),subQ0]});Q7=makeQuery(id+"F4.imprint","IMPRINT",FACE,{"disambiguationData":[TD([[makeQuery(id+"F4.imprint","IMPRINT",EDGE,{"disambiguationData":[TD([[subQ1,-1.0]])],"derivedFrom":subQ0}),1.0]])]});}
            var Q8;
            {var subQ0=sQuery(id+"F4.wireOp",EDGE,"E57");Q8=makeQuery(id+"F4.imprint","IMPRINT",FACE,{"disambiguationData":[TD([[makeQuery(id+"F4.imprint","IMPRINT",EDGE,{"derivedFrom":subQ0}),1.0]])]});}
            var Q9;
            {var subQ0=sQuery(id+"F4.wireOp",EDGE,"E48");var subQ1=sQuery(id+"F4.wireOp",EDGE,"E46");var subQ2=makeQuery(id+"F4.imprint","INTERSECT",VERTEX,{"disambiguationData":[OD(1.0)],"derivedFrom":[subQ1,subQ0]});Q9=makeQuery(id+"F4.imprint","IMPRINT",FACE,{"disambiguationData":[TD([[makeQuery(id+"F4.imprint","IMPRINT",EDGE,{"disambiguationData":[TD([[subQ2,-1.0]])],"derivedFrom":subQ1}),1.0]])]});}
            var Q10;
            {var subQ0=sQuery(id+"F4.wireOp",EDGE,"E49");var subQ1=sQuery(id+"F4.wireOp",EDGE,"E46");var subQ2=makeQuery(id+"F4.imprint","INTERSECT",VERTEX,{"derivedFrom":[subQ1,subQ0]});Q10=makeQuery(id+"F4.imprint","IMPRINT",FACE,{"disambiguationData":[TD([[makeQuery(id+"F4.imprint","IMPRINT",EDGE,{"disambiguationData":[TD([[subQ2,-1.0]])],"derivedFrom":subQ1}),1.0]])]});}
            var Q11;
            {var subQ0=sQuery(id+"F4.wireOp",EDGE,"E48");var subQ1=sQuery(id+"F4.wireOp",EDGE,"E45");var subQ2=makeQuery(id+"F4.imprint","INTERSECT",VERTEX,{"disambiguationData":[OD(0.0)],"derivedFrom":[subQ1,subQ0]});Q11=makeQuery(id+"F4.imprint","IMPRINT",FACE,{"disambiguationData":[TD([[makeQuery(id+"F4.imprint","IMPRINT",EDGE,{"disambiguationData":[TD([[subQ2,-1.0]])],"derivedFrom":subQ1}),-1.0]])]});}
            var Q12;
            {var subQ8=sQuery(id+"F4.wireOp",EDGE,"E28.0");Q12=makeQuery(id+"F4.imprint","IMPRINT",FACE,{"disambiguationData":[TD([[makeQuery(id+"F4.imprint","IMPRINT",EDGE,{"derivedFrom":subQ8}),1.0]])]});}
            var Q13;
            {var subQ0=sQuery(id+"F4.wireOp",EDGE,"E56");Q13=makeQuery(id+"F4.imprint","IMPRINT",FACE,{"disambiguationData":[TD([[makeQuery(id+"F4.imprint","IMPRINT",EDGE,{"derivedFrom":subQ0}),-1.0]])]});}
            var Q14;
            {var subQ2=sQuery(id+"F4.wireOp",EDGE,"E42.filletArc");var subQ4=sQuery(id+"F4.wireOp",EDGE,"E28.2");var subQ5=makeQuery(id+"F4.imprint","INTERSECT",VERTEX,{"derivedFrom":[subQ4,subQ2]});Q14=makeQuery(id+"F4.imprint","IMPRINT",FACE,{"disambiguationData":[TD([[makeQuery(id+"F4.imprint","IMPRINT",EDGE,{"disambiguationData":[TD([[subQ5,-1.0]])],"derivedFrom":subQ4}),-1.0]])]});}
            var Q15;
            {var subQ4=sQuery(id+"F4.wireOp",EDGE,"E28.2");var subQ6=sQuery(id+"F4.wireOp",EDGE,"E41.filletArc");var subQ7=makeQuery(id+"F4.imprint","INTERSECT",VERTEX,{"derivedFrom":[subQ4,subQ6]});Q15=makeQuery(id+"F4.imprint","IMPRINT",FACE,{"disambiguationData":[TD([[makeQuery(id+"F4.imprint","IMPRINT",EDGE,{"disambiguationData":[TD([[subQ7,1.0]])],"derivedFrom":subQ4}),-1.0]])]});}
            var Q16;
            {var subQ0=sQuery(id+"F4.wireOp",EDGE,"E43");var subQ1=sQuery(id+"F4.wireOp",EDGE,"E41.filletArc");var subQ2=makeQuery(id+"F4.imprint","INTERSECT",VERTEX,{"derivedFrom":[subQ1,subQ0]});Q16=makeQuery(id+"F4.imprint","IMPRINT",FACE,{"disambiguationData":[TD([[makeQuery(id+"F4.imprint","IMPRINT",EDGE,{"disambiguationData":[TD([[subQ2,-1.0]])],"derivedFrom":subQ1}),1.0]])]});}
            var Q17;
            {var subQ4=sQuery(id+"F4.wireOp",EDGE,"E41.filletArc");var subQ6=sQuery(id+"F4.wireOp",EDGE,"E28.5");var subQ7=makeQuery(id+"F4.imprint","INTERSECT",VERTEX,{"derivedFrom":[subQ6,subQ4]});Q17=makeQuery(id+"F4.imprint","IMPRINT",FACE,{"disambiguationData":[TD([[makeQuery(id+"F4.imprint","IMPRINT",EDGE,{"disambiguationData":[TD([[subQ7,-1.0]])],"derivedFrom":subQ6}),-1.0]])]});}
            var Q18;
            {var subQ2=sQuery(id+"F4.wireOp",EDGE,"E40.filletArc");var subQ6=sQuery(id+"F4.wireOp",EDGE,"E28.5");var subQ7=makeQuery(id+"F4.imprint","INTERSECT",VERTEX,{"derivedFrom":[subQ6,subQ2]});Q18=makeQuery(id+"F4.imprint","IMPRINT",FACE,{"disambiguationData":[TD([[makeQuery(id+"F4.imprint","IMPRINT",EDGE,{"disambiguationData":[TD([[subQ7,1.0]])],"derivedFrom":subQ6}),-1.0]])]});}
            var Q19;
            {var subQ0=sQuery(id+"F4.wireOp",EDGE,"E55");Q19=makeQuery(id+"F4.imprint","IMPRINT",FACE,{"disambiguationData":[TD([[makeQuery(id+"F4.imprint","IMPRINT",EDGE,{"derivedFrom":subQ0}),-1.0]])]});}
            var Q20;
            {var subQ0=sQuery(id+"F4.wireOp",EDGE,"E58");Q20=makeQuery(id+"F4.imprint","IMPRINT",FACE,{"disambiguationData":[TD([[makeQuery(id+"F4.imprint","IMPRINT",EDGE,{"derivedFrom":subQ0}),-1.0]])]});}
            var Q21;
            {var subQ4=sQuery(id+"F4.wireOp",EDGE,"E39.filletArc");var subQ6=sQuery(id+"F4.wireOp",EDGE,"E28.9");var subQ7=makeQuery(id+"F4.imprint","INTERSECT",VERTEX,{"derivedFrom":[subQ6,subQ4]});Q21=makeQuery(id+"F4.imprint","IMPRINT",FACE,{"disambiguationData":[TD([[makeQuery(id+"F4.imprint","IMPRINT",EDGE,{"disambiguationData":[TD([[subQ7,-1.0]])],"derivedFrom":subQ6}),-1.0]])]});}
            var Q22;
            {var subQ0=sQuery(id+"F4.wireOp",EDGE,"E57");Q22=makeQuery(id+"F4.imprint","IMPRINT",FACE,{"disambiguationData":[TD([[makeQuery(id+"F4.imprint","IMPRINT",EDGE,{"derivedFrom":subQ0}),-1.0]])]});}
            var Q23;
            {var subQ4=sQuery(id+"F4.wireOp",EDGE,"E37.filletArc");var subQ5=sQuery(id+"F4.wireOp",EDGE,"E28.11");var subQ6=makeQuery(id+"F4.imprint","INTERSECT",VERTEX,{"derivedFrom":[subQ5,subQ4]});Q23=makeQuery(id+"F4.imprint","IMPRINT",FACE,{"disambiguationData":[TD([[makeQuery(id+"F4.imprint","IMPRINT",EDGE,{"disambiguationData":[TD([[subQ6,1.0]])],"derivedFrom":subQ5}),-1.0]])]});}
            var Q24;
            {var subQ0=sQuery(id+"F4.wireOp",EDGE,"E47");var subQ1=sQuery(id+"F4.wireOp",EDGE,"E38.filletArc");var subQ2=makeQuery(id+"F4.imprint","INTERSECT",VERTEX,{"derivedFrom":[subQ1,subQ0]});Q24=makeQuery(id+"F4.imprint","IMPRINT",FACE,{"disambiguationData":[TD([[makeQuery(id+"F4.imprint","IMPRINT",EDGE,{"disambiguationData":[TD([[subQ2,-1.0]])],"derivedFrom":subQ1}),1.0]])]});}
            var Q25;
            {var subQ1=sQuery(id+"F4.wireOp",EDGE,"E38.filletArc");var subQ5=sQuery(id+"F4.wireOp",EDGE,"E28.11");var subQ8=makeQuery(id+"F4.imprint","INTERSECT",VERTEX,{"derivedFrom":[subQ5,subQ1]});Q25=makeQuery(id+"F4.imprint","IMPRINT",FACE,{"disambiguationData":[TD([[makeQuery(id+"F4.imprint","IMPRINT",EDGE,{"disambiguationData":[TD([[subQ8,-1.0]])],"derivedFrom":subQ5}),-1.0]])]});}
            var Q26;
            {var subQ1=sQuery(id+"F4.wireOp",EDGE,"E38.filletArc");var subQ4=sQuery(id+"F4.wireOp",EDGE,"E28.9");var subQ5=makeQuery(id+"F4.imprint","INTERSECT",VERTEX,{"derivedFrom":[subQ4,subQ1]});Q26=makeQuery(id+"F4.imprint","IMPRINT",FACE,{"disambiguationData":[TD([[makeQuery(id+"F4.imprint","IMPRINT",EDGE,{"disambiguationData":[TD([[subQ5,1.0]])],"derivedFrom":subQ4}),-1.0]])]});}
            extrude(context, id + "F6", {"entities" : qUnion([Q0, Q1, Q2, Q3, Q4, Q5, Q6, Q7, Q8, Q9, Q10, Q11, Q12, Q13, Q14, Q15, Q16, Q17, Q18, Q19, Q20, Q21, Q22, Q23, Q24, Q25, Q26]), "depth" : 6 * mm});
        }
        {
            var Q0;
            Q0=qCreatedBy(makeId("Front.planeOp"),FACE);
            var sketch = newSketch(context, id + "F7", { "sketchPlane" : qUnion([Q0])});
            skArc(sketch, "E61.0", {"start": v(-7.27, 65.18) * mm, "mid": v(-14.36, 4.25) * mm, "end": v(35.8, -31.07) * mm});
            skArc(sketch, "E62.0", {"start": v(-11.88, 192.18) * mm, "mid": v(-79.6, 132.68) * mm, "end": v(-11.88, 73.17) * mm});
            skArc(sketch, "E63.0", {"start": v(-7.27, 273.02) * mm, "mid": v(-19.6, 236.6) * mm, "end": v(-7.27, 200.17) * mm});
            skArc(sketch, "E64.0", {"start": v(-11.88, 400.02) * mm, "mid": v(-79.6, 340.52) * mm, "end": v(-11.88, 281.02) * mm});
            skArc(sketch, "E65.0", {"start": v(35.8, 504.27) * mm, "mid": v(-14.36, 468.95) * mm, "end": v(-7.27, 408.02) * mm});
            skLineSegment(sketch, "E66", {"start": v(40.4, -36.05) * mm, "end": v(40.4, -301.25) * mm});
            skLineSegment(sketch, "E67", {"start": v(40.4, -301.25) * mm, "end": v(20.4, -301.25) * mm});
            skLineSegment(sketch, "E68", {"start": v(20.4, -301.25) * mm, "end": v(20.4, -48.7) * mm});
            skArc(sketch, "E69", {"start": v(40.4, 524.44) * mm, "mid": v(-24.55, 491.13) * mm, "end": v(-35.42, 418.94) * mm});
            skLineSegment(sketch, "E70", {"start": v(40.4, 509.25) * mm, "end": v(40.4, 524.44) * mm});
            skArc(sketch, "E71.trimOffspring", {"start": v(-35.42, 211.1) * mm, "mid": v(-99.6, 132.68) * mm, "end": v(-35.42, 54.26) * mm});
            skArc(sketch, "E72.trimOffspring", {"start": v(-35.42, 54.26) * mm, "mid": v(-29.92, -9.38) * mm, "end": v(20.4, -48.7) * mm});
            skArc(sketch, "E73.trimOffspring", {"start": v(-35.42, 262.1) * mm, "mid": v(-39.6, 236.6) * mm, "end": v(-35.42, 211.1) * mm});
            skArc(sketch, "E74.trimOffspring", {"start": v(-35.42, 418.94) * mm, "mid": v(-99.6, 340.52) * mm, "end": v(-35.42, 262.1) * mm});
            skPoint(sketch, "E75.visualSharp", {"position": v(10.4, 80.71) * mm});
            skArc(sketch, "E75.filletArc", {"start": v(-7.27, 65.18) * mm, "mid": v(-6.91, 70.71) * mm, "end": v(-11.88, 73.17) * mm});
            skPoint(sketch, "E76.visualSharp", {"position": v(10.4, 184.64) * mm});
            skArc(sketch, "E76.filletArc", {"start": v(-11.88, 192.18) * mm, "mid": v(-6.91, 194.64) * mm, "end": v(-7.27, 200.17) * mm});
            skPoint(sketch, "E77.visualSharp", {"position": v(10.4, 288.56) * mm});
            skArc(sketch, "E77.filletArc", {"start": v(-7.27, 273.02) * mm, "mid": v(-6.91, 278.56) * mm, "end": v(-11.88, 281.02) * mm});
            skPoint(sketch, "E78.visualSharp", {"position": v(10.4, 392.48) * mm});
            skArc(sketch, "E78.filletArc", {"start": v(-11.88, 400.02) * mm, "mid": v(-6.91, 402.48) * mm, "end": v(-7.27, 408.02) * mm});
            skPoint(sketch, "E79.visualSharp", {"position": v(40.4, -31.25) * mm});
            skArc(sketch, "E79.filletArc", {"start": v(40.4, -36.05) * mm, "mid": v(39.08, -32.66) * mm, "end": v(35.8, -31.07) * mm});
            skPoint(sketch, "E80.visualSharp", {"position": v(40.4, 504.44) * mm});
            skArc(sketch, "E80.filletArc", {"start": v(35.8, 504.27) * mm, "mid": v(39.08, 505.86) * mm, "end": v(40.4, 509.25) * mm});
            skCircle(sketch, "E81", {"center": v(30.4, -174.98) * mm, "radius": 4 * mm});
            skPoint(sketch, "E81.centerSnap0", {"position": v(30.4, -301.25) * mm});
            skPoint(sketch, "E81.centerSnap1", {"position": v(20.4, -174.98) * mm});
            skLineSegment(sketch, "E82", {"start": v(-35.42, 54.26) * mm, "end": v(10.4, 80.71) * mm, "construction": true});
            skLineSegment(sketch, "E83", {"start": v(-35.42, 418.94) * mm, "end": v(10.4, 392.48) * mm, "construction": true});
            skCircle(sketch, "E84", {"center": v(-20.82, 62.69) * mm, "radius": 4 * mm});
            skCircle(sketch, "E85", {"center": v(-20.82, 410.51) * mm, "radius": 4 * mm});
            skLineSegment(sketch, "E86", {"start": v(-20.82, 62.69) * mm, "end": v(-20.82, 410.51) * mm, "construction": true});
            skCircle(sketch, "E87", {"center": v(30.4, -199.98) * mm, "radius": 2.5 * mm});
            skCircle(sketch, "E88", {"center": v(30.4, -149.98) * mm, "radius": 2.5 * mm});
            skLineSegment(sketch, "E89", {"start": v(30.4, -199.98) * mm, "end": v(30.4, -174.98) * mm, "construction": true});
            skLineSegment(sketch, "E90", {"start": v(30.4, -174.98) * mm, "end": v(30.4, -149.98) * mm, "construction": true});
            skCircle(sketch, "E91", {"center": v(40.4, 28.75) * mm, "radius": 70 * mm, "construction": true});
            skCircle(sketch, "E92", {"center": v(-19.6, 340.52) * mm, "radius": 70 * mm, "construction": true});
            skCircle(sketch, "E93", {"center": v(-29.55, 26.38) * mm, "radius": 2.5 * mm});
            skCircle(sketch, "E94.MirrorC", {"center": v(-56.62, 73.27) * mm, "radius": 2.5 * mm});
            skCircle(sketch, "E95", {"center": v(-56.62, 399.92) * mm, "radius": 2.5 * mm});
            skCircle(sketch, "E96.MirrorC", {"center": v(-29.55, 446.81) * mm, "radius": 2.5 * mm});
            skLineSegment(sketch, "E97", {"start": v(-56.62, 73.27) * mm, "end": v(-56.62, 399.92) * mm, "construction": true});
            skSolve(sketch);
        }
        {
            var Q0;
            Q0=makeQuery(id+"F7.imprint","IMPRINT",FACE,{"disambiguationData":[TD([[makeQuery(id+"F7.imprint","IMPRINT",EDGE,{"derivedFrom":sQuery(id+"F7.wireOp",EDGE,"E61.0")}),-1.0]])]});
            extrude(context, id + "F8", {"entities" : qUnion([Q0]), "depth" : 6 * mm});
        }
    });
